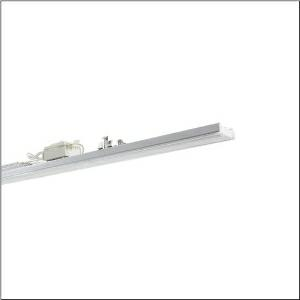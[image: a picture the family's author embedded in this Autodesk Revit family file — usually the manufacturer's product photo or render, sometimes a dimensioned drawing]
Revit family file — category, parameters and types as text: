
# Revit family: licross_11_recessed_extreme_mo_51te12dn4axge
name_source: partatom
category: Lighting Fixtures
units: mm (PartAtom-declared; Revit-internal decimal feet)

## family parameters
Cut with Voids When Loaded = No
Host = Face
Light Source = No
Part Type = Normal
Room Calculation Point = No
Round Connector Dimension = Use Diameter
Shared = No

## types (1)
- --- (1 x LED, 10240 lm, 56.7 W, 4000K)
    Apparent Load = 57 VA
    CIE Flux Codes = 67 92 99 100 100
    Color Rendering = 80
    Color Temperature = 4000K
    Default Elevation = 1800 mm
    Description = Licross 11 Recessed extreme MO, luminaire insert, of sheet steel, galvanised, coil coated, white, length: 1.500mm, width: 66mm, height: 67mm, LED rated luminous flux: 10.240lm, light colour: 840, SDCM (Standard Deviation of Colour Matching)MacAdam ≤ 2 SDCM (initial), control gear: DALI 2, with plug, 5-pole, with phase selection, mains connection: 220..240V, AC, 50/60Hz, rated input power: 57W, internal wiring halogen-free, primary optical cover: cover, of PMMA, light emission: direct distribution, primary light characteristic: symmetric, protection rating (complete): IP54, insulation class (complete): insulation class I (protective earthing), certification: CE, ENEC, VDE, UKCA, protection symbol: D if used in an environment with non-conductive dust loads with corresponding accessories, impact resistance: IK06, permissible ambient temperature for indoor applications: -40..+45°C, corresponds to IFS (International Featured Standards) requirements for safety and quality in the food industry, reducing of maximum allowable ambient temperature of 5°C with ceiling mounting, LABS conformity tested according to VDMA 24364:2018-05, The light source and the operating device comply with the requirements of the Ecodesign Regulation (EU) 2019/2020 and are replaceable in accordance with this regulation, packaging unit: 1 piece
    Height = 58 mm
    Lamp = 1 x LED
    Lamp Light Flux = 10240 lm
    Lamp Power = 56.7 W
    Lamp count = 1
    Length = 1500 mm
    Luminous efficacy = 181 lm/W
    Manufacturer = Siteco
    ModVariant = No
    Model = 51TE12DN4AXGE
    Mounting Place = Ceiling
    Mounting Type = Pendant
    Number of Poles = 1
    OnlyDefault = Yes
    Power Factor = 1
    Product Name = Licross 11 Recessed extreme MO
    Product group = luminaire insert | ceiling pendant
    ProductGroupID = 901
    Protection Class = Protection class I
    Protection Degree = IP 54
    RLX_Detail_Level = 1
    RLX_Emergency_Light_Flux = 0 lm
    RLX_Emergency_Type = 0
    RLX_Emergency_Type_DB = No
    RlxData = <blob elided: 24673 chars, md5=f24bbb7f>
    Socket = socket
    Standby Power = 0 W
    System Light Flux = 10240 lm
    System Power = 57 W
    Type Comments = factory setting: luminous flux: 100 % | dim-lin: 254 | 378 mA
    Type Image = l_1296930.jpg
    URL = http://relux.com
    VarID = @adj_087575
    Voltage = 0 V
    Weight = 0.00 kg
    Width = 66 mm

## geometry (parser evidence)
native form markers: Blend x4, Sweep x11
no freeform markers — native parametric forms only
